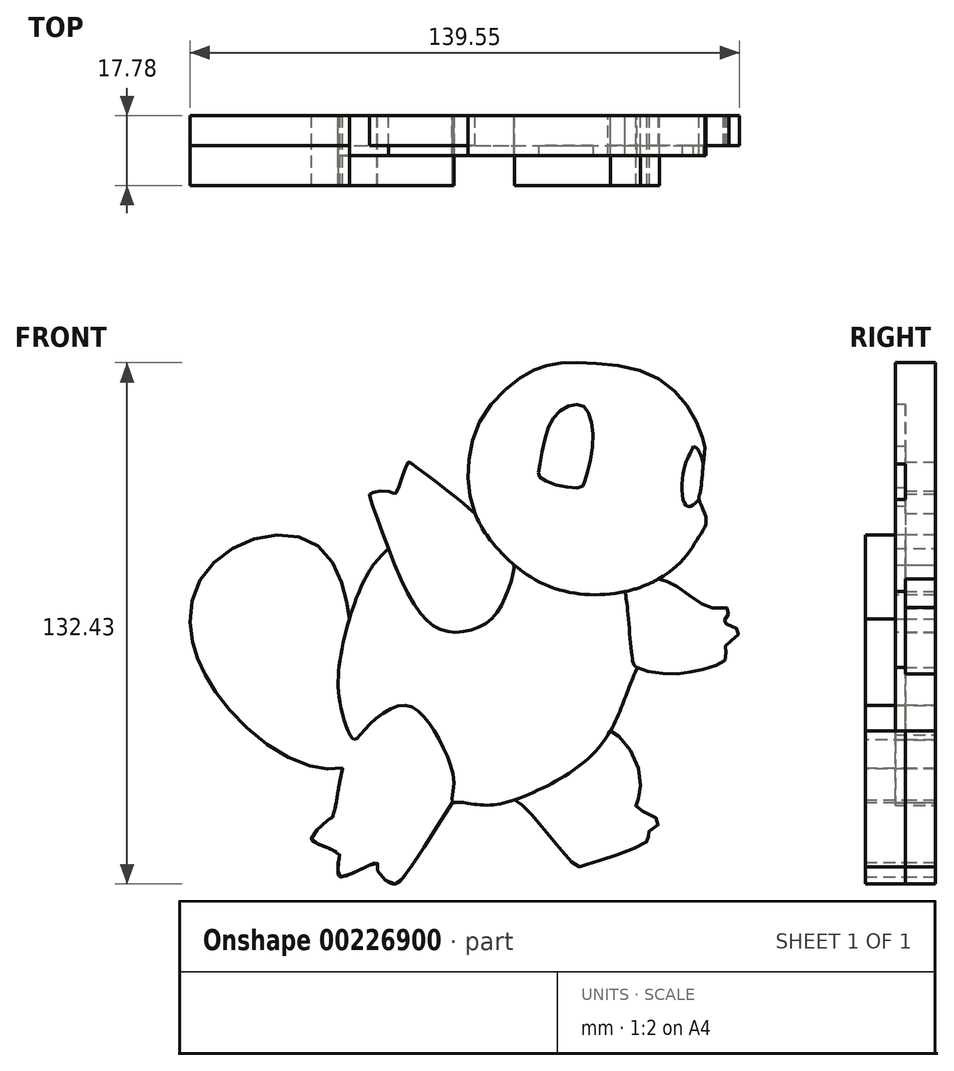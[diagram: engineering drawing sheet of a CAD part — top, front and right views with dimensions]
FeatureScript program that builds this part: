
annotation { "Feature Type Name" : "Feature", "Feature Type Description" : "" }
export const myFeature = defineFeature(function(context is Context, id is Id, definition is map)
    precondition{}
    {
        {
            var Q0;
            Q0=qCreatedBy(makeId("Front.planeOp"),FACE);
            var sketch = newSketch(context, id + "F0", { "sketchPlane" : qUnion([Q0])});
            skFitSpline(sketch, "E0", {"points": [v(29.05, 56) * mm, v(22.12, 53.02) * mm, v(12.18, 42.98) * mm, v(8.46, 29.93) * mm, v(10.17, 18.28) * mm, v(17.4, 7.74) * mm, v(28.44, 0) * mm, v(41.09, -2.4) * mm, v(53.44, 0) * mm, v(62.77, 6.24) * mm, v(67.3, 12.66) * mm, v(68.9, 16.78) * mm, v(67.1, 21.8) * mm, v(67.4, 23.6) * mm, v(68.34, 32.84) * mm, v(68.53, 34.17) * mm, v(68.4, 36.05) * mm, v(64.58, 44.79) * mm, v(54.44, 53.72) * mm, v(37.98, 56.53) * mm, v(29.05, 56) * mm]});
            skFitSpline(sketch, "E1", {"points": [v(26.6, 27.48) * mm, v(31.75, 25.29) * mm, v(37.24, 25.04) * mm, v(38.25, 26.8) * mm, v(40.02, 35.25) * mm, v(39.1, 43.7) * mm, v(36.48, 45.97) * mm, v(31.75, 44.28) * mm, v(28.2, 38.29) * mm, v(26.43, 29.17) * mm, v(26.6, 27.48) * mm]});
            skFitSpline(sketch, "E2", {"points": [v(65.73, 35.35) * mm, v(64.55, 32.98) * mm, v(63.22, 29.33) * mm, v(63.22, 21.32) * mm, v(64.83, 20.04) * mm, v(66.58, 21.32) * mm, v(67.1, 21.8) * mm], "startDerivative": vector(-7.36, -14.66) * mm, "endDerivative": vector(5.08, 4.47) * mm});
            skFitSpline(sketch, "E3", {"points": [v(65.73, 35.35) * mm, v(67.1, 34.17) * mm, v(68.17, 30.78) * mm, v(68.16, 30.64) * mm], "startDerivative": vector(3.81, -1.87) * mm, "endDerivative": vector(-0.27, -0.76) * mm});
            skFitSpline(sketch, "E4", {"points": [v(10.17, 18.28) * mm, v(3.6, 23.74) * mm, v(-6.31, 31.18) * mm, v(-6.99, 31.06) * mm, v(-9.92, 23.29) * mm, v(-10.82, 23.63) * mm, v(-16.34, 23.4) * mm, v(-16.34, 21.8) * mm, v(-7.89, 0) * mm, v(0, -10.52) * mm, v(6.3, -11.87) * mm, v(13.07, -9.61) * mm, v(17.35, -4.2) * mm, v(19.94, 3.34) * mm, v(20.12, 5.23) * mm], "startDerivative": vector(-66.52, 57.12) * mm, "endDerivative": vector(0.26, 39.3) * mm});
            skFitSpline(sketch, "E5", {"points": [v(48.34, -1.58) * mm, v(48.94, -6.1) * mm, v(50.1, -18.44) * mm, v(51.39, -20.9) * mm, v(60.21, -22.49) * mm, v(68.53, -21.2) * mm, v(73.93, -18.66) * mm, v(73.72, -15.9) * mm, v(75.2, -14.08) * mm, v(77.29, -11.53) * mm, v(73.4, -9.51) * mm, v(73.83, -8.66) * mm, v(74.57, -6.1) * mm, v(72.66, -5.68) * mm, v(69.57, -5.58) * mm, v(60.96, 0) * mm, v(56.86, 1.66) * mm], "startDerivative": vector(9.15, -57.01) * mm, "endDerivative": vector(-58, 15.23) * mm});
            skFitSpline(sketch, "E6", {"points": [v(-11.8, 9.31) * mm, v(-16.41, 4.02) * mm, v(-21.72, -8.48) * mm, v(-24.37, -21.18) * mm, v(-23.8, -31.42) * mm, v(-20.58, -39.19) * mm, v(-19.07, -38.05) * mm, v(-14.7, -33.69) * mm, v(-7.89, -30.47) * mm, v(-2.96, -33.12) * mm, v(2.16, -41.27) * mm, v(4.81, -50.56) * mm, v(4.43, -55.1) * mm, v(5.76, -55.1) * mm, v(13.34, -55.86) * mm, v(24.9, -52.64) * mm, v(35.51, -46.77) * mm, v(43.85, -38.24) * mm, v(48.97, -26.87) * mm, v(51.39, -20.9) * mm], "startDerivative": vector(-96.77, -91.17) * mm, "endDerivative": vector(47.87, 114.08) * mm});
            skFitSpline(sketch, "E7", {"points": [v(-20.58, -39.19) * mm, v(-23.43, -46.39) * mm, v(-25.9, -58.7) * mm, v(-26.65, -59.27) * mm, v(-31.2, -63.82) * mm, v(-30.82, -65.15) * mm, v(-24.37, -68.18) * mm, v(-24.37, -69.7) * mm, v(-24.56, -73.3) * mm, v(-23.43, -74.06) * mm, v(-14.7, -70.45) * mm, v(-14.7, -71.97) * mm, v(-10.82, -75.8) * mm, v(-7.89, -74.06) * mm, v(4.43, -55.1) * mm], "startDerivative": vector(-33.9, -64.3) * mm, "endDerivative": vector(94.94, 152.63) * mm});
            skFitSpline(sketch, "E8", {"points": [v(20.18, -54.53) * mm, v(24.52, -58.14) * mm, v(35.89, -71.21) * mm, v(37.78, -71.21) * mm, v(48.2, -67.8) * mm, v(54.46, -64.2) * mm, v(53.9, -63.06) * mm, v(57.11, -60.22) * mm, v(51.39, -56.62) * mm, v(51.39, -55.1) * mm, v(51.39, -45.44) * mm, v(44.62, -36.94) * mm, v(43.97, -38.05) * mm], "startDerivative": vector(43.02, -26.8) * mm, "endDerivative": vector(-6.42, -41.97) * mm});
            skFitSpline(sketch, "E9", {"points": [v(-23.43, -46.39) * mm, v(-29.68, -46.39) * mm, v(-42, -40.9) * mm, v(-53.75, -29.7) * mm, v(-59.24, -20.9) * mm, v(-61.7, -13.6) * mm, v(-61.33, -2.4) * mm, v(-53.75, 7.81) * mm, v(-41.05, 12.74) * mm, v(-29.68, 10.09) * mm, v(-23.43, 0) * mm, v(-21.72, -8.48) * mm], "startDerivative": vector(-84.41, -9.39) * mm, "endDerivative": vector(13.47, -101.04) * mm});
            skSolve(sketch);
        }
        {
            var Q0;
            Q0=makeQuery(id+"F0.imprint","IMPRINT",FACE,{"disambiguationData":[TD([[makeQuery(id+"F0.imprint","IMPRINT",EDGE,{"derivedFrom":sQuery(id+"F0.wireOp",EDGE,"E1")}),-1.0]])]});
            extrude(context, id + "F1", {"entities" : qUnion([Q0]), "depth" : 10.16 * mm});
        }
        {
            var Q0;
            {var subQ0=sQuery(id+"F0.wireOp",EDGE,"E2");Q0=makeQuery(id+"F0.imprint","IMPRINT",FACE,{"disambiguationData":[TD([[makeQuery(id+"F0.imprint","IMPRINT",EDGE,{"derivedFrom":subQ0}),1.0]])]});}
            var Q1;
            Q1=makeQuery(id+"F0.imprint","IMPRINT",FACE,{"disambiguationData":[TD([[makeQuery(id+"F0.imprint","IMPRINT",EDGE,{"derivedFrom":sQuery(id+"F0.wireOp",EDGE,"E1")}),1.0]])]});
            extrude(context, id + "F2", {"entities" : qUnion([Q0, Q1]), "operationType" : NewBodyOperationType.ADD, "depth" : 7.62 * mm});
        }
        {
            var Q0;
            {var subQ0=sQuery(id+"F0.wireOp",EDGE,"E4");var subQ1=sQuery(id+"F0.wireOp",EDGE,"E0");var subQ2=makeQuery(id+"F0.imprint","INTERSECT",VERTEX,{"disambiguationData":[OD(0.0)],"derivedFrom":[subQ1,subQ0]});Q0=makeQuery(id+"F0.imprint","IMPRINT",FACE,{"disambiguationData":[TD([[makeQuery(id+"F0.imprint","IMPRINT",EDGE,{"disambiguationData":[TD([[subQ2,-1.0]])],"derivedFrom":subQ1}),-1.0]])]});}
            var Q1;
            {var subQ0=sQuery(id+"F0.wireOp",EDGE,"E5");var subQ1=sQuery(id+"F0.wireOp",EDGE,"E0");var subQ2=makeQuery(id+"F0.imprint","INTERSECT",VERTEX,{"disambiguationData":[OD(0.0)],"derivedFrom":[subQ1,subQ0]});Q1=makeQuery(id+"F0.imprint","IMPRINT",FACE,{"disambiguationData":[TD([[makeQuery(id+"F0.imprint","IMPRINT",EDGE,{"disambiguationData":[TD([[subQ2,-1.0]])],"derivedFrom":subQ1}),-1.0]])]});}
            var Q2;
            {var subQ0=sQuery(id+"F0.wireOp",EDGE,"E8");var subQ1=sQuery(id+"F0.wireOp",EDGE,"E6");var subQ2=makeQuery(id+"F0.imprint","INTERSECT",VERTEX,{"disambiguationData":[OD(0.0)],"derivedFrom":[subQ1,subQ0]});Q2=makeQuery(id+"F0.imprint","IMPRINT",FACE,{"disambiguationData":[TD([[makeQuery(id+"F0.imprint","IMPRINT",EDGE,{"disambiguationData":[TD([[subQ2,-1.0]])],"derivedFrom":subQ1}),-1.0]])]});}
            var Q3;
            {var subQ0=sQuery(id+"F0.wireOp",EDGE,"E7");var subQ1=sQuery(id+"F0.wireOp",EDGE,"E6");var subQ2=makeQuery(id+"F0.imprint","INTERSECT",VERTEX,{"disambiguationData":[OD(0.0)],"derivedFrom":[subQ1,subQ0]});Q3=makeQuery(id+"F0.imprint","IMPRINT",FACE,{"disambiguationData":[TD([[makeQuery(id+"F0.imprint","IMPRINT",EDGE,{"disambiguationData":[TD([[subQ2,-1.0]])],"derivedFrom":subQ1}),-1.0]])]});}
            var Q4;
            {var subQ3=sQuery(id+"F0.wireOp",EDGE,"E9");Q4=makeQuery(id+"F0.imprint","IMPRINT",FACE,{"disambiguationData":[TD([[makeQuery(id+"F0.imprint","IMPRINT",EDGE,{"derivedFrom":subQ3}),-1.0]])]});}
            extrude(context, id + "F3", {"entities" : qUnion([Q0, Q1, Q2, Q3, Q4]), "operationType" : NewBodyOperationType.ADD, "depth" : 7.62 * mm});
        }
        {
            var Q0;
            {var subQ1=sQuery(id+"F0.wireOp",EDGE,"E4");var subQ5=sQuery(id+"F0.wireOp",EDGE,"E0");var subQ11=makeQuery(id+"F0.imprint","INTERSECT",VERTEX,{"disambiguationData":[OD(1.0)],"derivedFrom":[subQ5,subQ1]});Q0=makeQuery(id+"F0.imprint","IMPRINT",FACE,{"disambiguationData":[TD([[makeQuery(id+"F0.imprint","IMPRINT",EDGE,{"disambiguationData":[TD([[subQ11,-1.0]])],"derivedFrom":subQ5}),-1.0]])]});}
            extrude(context, id + "F4", {"entities" : qUnion([Q0]), "depth" : 10.16 * mm});
        }
        {
            var Q0;
            Q0=makeQuery(id+"F3.opExtrude","CAP_FACE",FACE,{"disambiguationData":[OSD([sQuery(id+"F0.wireOp",EDGE,"E6"),sQuery(id+"F0.wireOp",EDGE,"E7"),sQuery(id+"F0.wireOp",EDGE,"E9")])],"isStart":false});
            var Q1;
            Q1=makeQuery(id+"F3.opExtrude","CAP_FACE",FACE,{"disambiguationData":[OSD([sQuery(id+"F0.wireOp",EDGE,"E6"),sQuery(id+"F0.wireOp",EDGE,"E8")])],"isStart":false});
            extrude(context, id + "F5", {"entities" : qUnion([Q0, Q1]), "depth" : 10.16 * mm});
        }
    });
